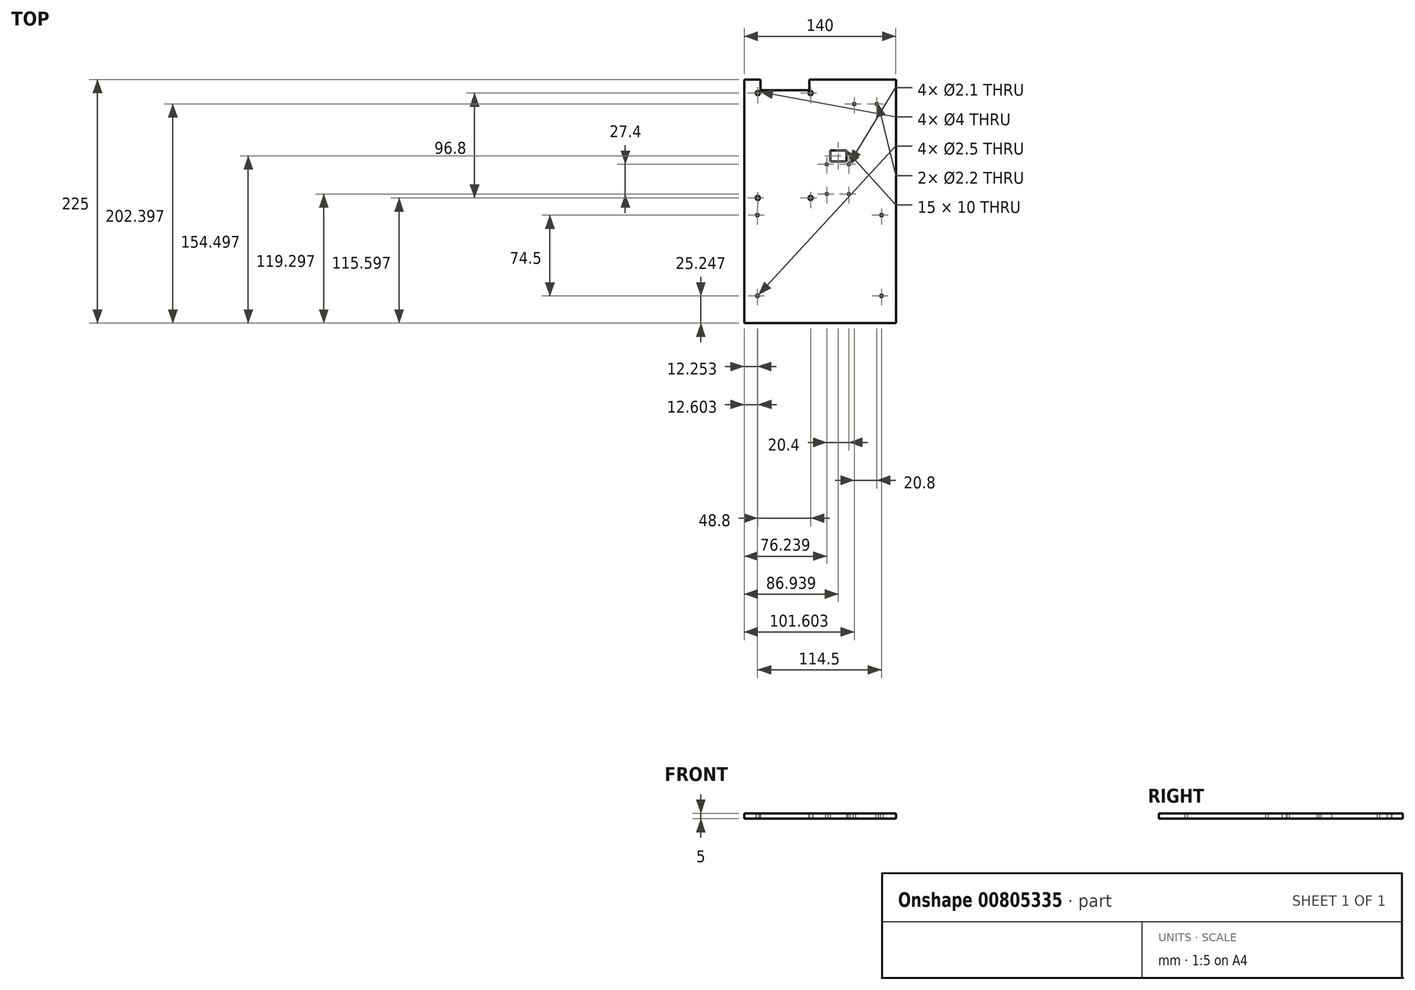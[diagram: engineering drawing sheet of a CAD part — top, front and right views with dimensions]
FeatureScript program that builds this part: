
annotation { "Feature Type Name" : "Feature", "Feature Type Description" : "" }
export const myFeature = defineFeature(function(context is Context, id is Id, definition is map)
    precondition{}
    {
        {
            var Q0;
            Q0=qCreatedBy(makeId("Top.planeOp"),FACE);
            var sketch = newSketch(context, id + "F0", { "sketchPlane" : qUnion([Q0])});
            skLineSegment(sketch, "E0.bottom", {"start": v(-96.6, 98.7) * mm, "end": v(43.4, 98.7) * mm});
            skLineSegment(sketch, "E0.top", {"start": v(-96.6, -126.3) * mm, "end": v(43.4, -126.3) * mm});
            skLineSegment(sketch, "E0.left", {"start": v(-96.6, 98.7) * mm, "end": v(-96.6, -126.3) * mm});
            skLineSegment(sketch, "E0.right", {"start": v(43.4, 98.7) * mm, "end": v(43.4, -126.3) * mm});
            skLineSegment(sketch, "E1.bottom", {"start": v(-86.6, 88.7) * mm, "end": v(-32.6, 88.7) * mm});
            skLineSegment(sketch, "E1.top", {"start": v(-86.6, -13.3) * mm, "end": v(-32.6, -13.3) * mm});
            skLineSegment(sketch, "E1.left", {"start": v(-86.6, 88.7) * mm, "end": v(-86.6, -13.3) * mm});
            skLineSegment(sketch, "E1.right", {"start": v(-32.6, 88.7) * mm, "end": v(-32.6, -13.3) * mm});
            skLineSegment(sketch, "E2.bottom", {"start": v(-87.6, -23.3) * mm, "end": v(33.4, -23.3) * mm});
            skLineSegment(sketch, "E2.top", {"start": v(-87.6, -104.3) * mm, "end": v(33.4, -104.3) * mm});
            skLineSegment(sketch, "E2.left", {"start": v(-87.6, -23.3) * mm, "end": v(-87.6, -104.3) * mm});
            skLineSegment(sketch, "E2.right", {"start": v(33.4, -23.3) * mm, "end": v(33.4, -104.3) * mm});
            skLineSegment(sketch, "E3.bottom", {"start": v(-23.16, 23.2) * mm, "end": v(2.84, 23.2) * mm});
            skLineSegment(sketch, "E3.top", {"start": v(-23.16, -9.8) * mm, "end": v(2.84, -9.8) * mm});
            skLineSegment(sketch, "E3.left", {"start": v(-23.16, 23.2) * mm, "end": v(-23.16, -9.8) * mm});
            skLineSegment(sketch, "E3.right", {"start": v(2.84, 23.2) * mm, "end": v(2.84, -9.8) * mm});
            skLineSegment(sketch, "E4.bottom", {"start": v(2.4, 78.7) * mm, "end": v(28.4, 78.7) * mm});
            skLineSegment(sketch, "E4.top", {"start": v(2.4, 43.2) * mm, "end": v(28.4, 43.2) * mm});
            skLineSegment(sketch, "E4.left", {"start": v(2.4, 78.7) * mm, "end": v(2.4, 43.2) * mm});
            skLineSegment(sketch, "E4.right", {"start": v(28.4, 78.7) * mm, "end": v(28.4, 43.2) * mm});
            skLineSegment(sketch, "E5", {"start": v(2.84, 23.2) * mm, "end": v(-2.16, 23.2) * mm});
            skLineSegment(sketch, "E6", {"start": v(-2.16, 23.2) * mm, "end": v(-17.16, 23.2) * mm});
            skLineSegment(sketch, "E7", {"start": v(-2.16, 23.2) * mm, "end": v(-2.16, 33.2) * mm});
            skLineSegment(sketch, "E8.bottom", {"start": v(-17.16, 23.2) * mm, "end": v(-2.16, 23.2) * mm});
            skLineSegment(sketch, "E8.top", {"start": v(-17.16, 33.2) * mm, "end": v(-2.16, 33.2) * mm});
            skLineSegment(sketch, "E8.left", {"start": v(-17.16, 23.2) * mm, "end": v(-17.16, 33.2) * mm});
            skLineSegment(sketch, "E9.bottom", {"start": v(-81.6, 98.7) * mm, "end": v(-36.6, 98.7) * mm});
            skLineSegment(sketch, "E9.top", {"start": v(-81.6, 88.7) * mm, "end": v(-36.6, 88.7) * mm});
            skLineSegment(sketch, "E9.left", {"start": v(-81.6, 98.7) * mm, "end": v(-81.6, 88.7) * mm});
            skLineSegment(sketch, "E9.right", {"start": v(-36.6, 98.7) * mm, "end": v(-36.6, 88.7) * mm});
            skLineSegment(sketch, "E10", {"start": v(33.4, -23.3) * mm, "end": v(33.4, -43.3) * mm});
            skLineSegment(sketch, "E11.bottom", {"start": v(33.4, -43.3) * mm, "end": v(43.4, -43.3) * mm});
            skLineSegment(sketch, "E11.top", {"start": v(33.4, -23.3) * mm, "end": v(43.4, -23.3) * mm});
            skLineSegment(sketch, "E11.left", {"start": v(33.4, -43.3) * mm, "end": v(33.4, -23.3) * mm});
            skLineSegment(sketch, "E11.right", {"start": v(43.4, -43.3) * mm, "end": v(43.4, -23.3) * mm});
            skCircle(sketch, "E12", {"center": v(-84.35, -101.04) * mm, "radius": 1.25 * mm});
            skCircle(sketch, "E13", {"center": v(-84.35, -26.54) * mm, "radius": 1.25 * mm});
            skCircle(sketch, "E14", {"center": v(30.15, -26.54) * mm, "radius": 1.25 * mm});
            skCircle(sketch, "E15", {"center": v(30.15, -101.04) * mm, "radius": 1.25 * mm});
            skCircle(sketch, "E16", {"center": v(5, 76.1) * mm, "radius": 1.1 * mm});
            skCircle(sketch, "E17", {"center": v(25.8, 76.1) * mm, "radius": 1.1 * mm});
            skCircle(sketch, "E18", {"center": v(0.04, 20.4) * mm, "radius": 1.05 * mm});
            skCircle(sketch, "E19", {"center": v(0.04, -7) * mm, "radius": 1.05 * mm});
            skCircle(sketch, "E20", {"center": v(-20.36, -7) * mm, "radius": 1.05 * mm});
            skCircle(sketch, "E21", {"center": v(-20.36, 20.4) * mm, "radius": 1.05 * mm});
            skLineSegment(sketch, "E22.bottom", {"start": v(-86.6, 88.7) * mm, "end": v(-84.4, 88.7) * mm});
            skLineSegment(sketch, "E22.left", {"start": v(-86.6, 88.7) * mm, "end": v(-86.6, 86.5) * mm});
            skLineSegment(sketch, "E23.bottom", {"start": v(-86.6, 88.7) * mm, "end": v(-84, 88.7) * mm});
            skLineSegment(sketch, "E23.left", {"start": v(-86.6, 88.7) * mm, "end": v(-86.6, 86.1) * mm});
            skCircle(sketch, "E24", {"center": v(-84, 86.1) * mm, "radius": 2 * mm});
            skLineSegment(sketch, "E25.bottom", {"start": v(-32.6, 88.7) * mm, "end": v(-35.2, 88.7) * mm});
            skLineSegment(sketch, "E25.left", {"start": v(-32.6, 88.7) * mm, "end": v(-32.6, 86.1) * mm});
            skCircle(sketch, "E26", {"center": v(-35.2, 86.1) * mm, "radius": 2 * mm});
            skLineSegment(sketch, "E27.bottom", {"start": v(-32.6, -13.3) * mm, "end": v(-35.2, -13.3) * mm});
            skLineSegment(sketch, "E27.left", {"start": v(-32.6, -13.3) * mm, "end": v(-32.6, -10.7) * mm});
            skLineSegment(sketch, "E28.bottom", {"start": v(-86.6, -13.3) * mm, "end": v(-84, -13.3) * mm});
            skLineSegment(sketch, "E28.left", {"start": v(-86.6, -13.3) * mm, "end": v(-86.6, -10.7) * mm});
            skCircle(sketch, "E29", {"center": v(-84, -10.7) * mm, "radius": 2 * mm});
            skCircle(sketch, "E30", {"center": v(-35.2, -10.7) * mm, "radius": 2 * mm});
            skSolve(sketch);
        }
        {
            var Q0;
            Q0=makeQuery(id+"F0.imprint","IMPRINT",FACE,{"disambiguationData":[TD([[makeQuery(id+"F0.imprint","IMPRINT",EDGE,{"derivedFrom":sQuery(id+"F0.wireOp",EDGE,"E2.bottom")}),-1.0]])]});
            var Q1;
            {var subQ1=sQuery(id+"F0.wireOp",EDGE,"E0.top");Q1=makeQuery(id+"F0.imprint","IMPRINT",FACE,{"disambiguationData":[TD([[makeQuery(id+"F0.imprint","IMPRINT",EDGE,{"derivedFrom":subQ1}),1.0]])]});}
            var Q2;
            Q2=makeQuery(id+"F0.imprint","IMPRINT",FACE,{"disambiguationData":[TD([[makeQuery(id+"F0.imprint","IMPRINT",EDGE,{"derivedFrom":sQuery(id+"F0.wireOp",EDGE,"E1.top")}),1.0]])]});
            var Q3;
            Q3=makeQuery(id+"F0.imprint","IMPRINT",FACE,{"disambiguationData":[TD([[makeQuery(id+"F0.imprint","IMPRINT",EDGE,{"derivedFrom":sQuery(id+"F0.wireOp",EDGE,"E3.bottom")}),-1.0]])]});
            var Q4;
            Q4=makeQuery(id+"F0.imprint","IMPRINT",FACE,{"disambiguationData":[TD([[makeQuery(id+"F0.imprint","IMPRINT",EDGE,{"derivedFrom":sQuery(id+"F0.wireOp",EDGE,"E8.bottom")}),1.0]])]});
            var Q5;
            Q5=makeQuery(id+"F0.imprint","IMPRINT",FACE,{"disambiguationData":[TD([[makeQuery(id+"F0.imprint","IMPRINT",EDGE,{"derivedFrom":sQuery(id+"F0.wireOp",EDGE,"E4.bottom")}),-1.0]])]});
            var Q6;
            Q6=makeQuery(id+"F0.imprint","IMPRINT",FACE,{"disambiguationData":[TD([[makeQuery(id+"F0.imprint","IMPRINT",EDGE,{"derivedFrom":sQuery(id+"F0.wireOp",EDGE,"E11.bottom")}),1.0]])]});
            var Q7;
            Q7=makeQuery(id+"F0.imprint","IMPRINT",FACE,{"disambiguationData":[TD([[makeQuery(id+"F0.imprint","IMPRINT",EDGE,{"derivedFrom":sQuery(id+"F0.wireOp",EDGE,"E9.bottom")}),-1.0]])]});
            extrude(context, id + "F1", {"entities" : qUnion([Q0, Q1, Q2, Q3, Q4, Q5, Q6, Q7]), "depth" : 5 * mm, "offsetDistance" : 25 * mm});
        }
    });
